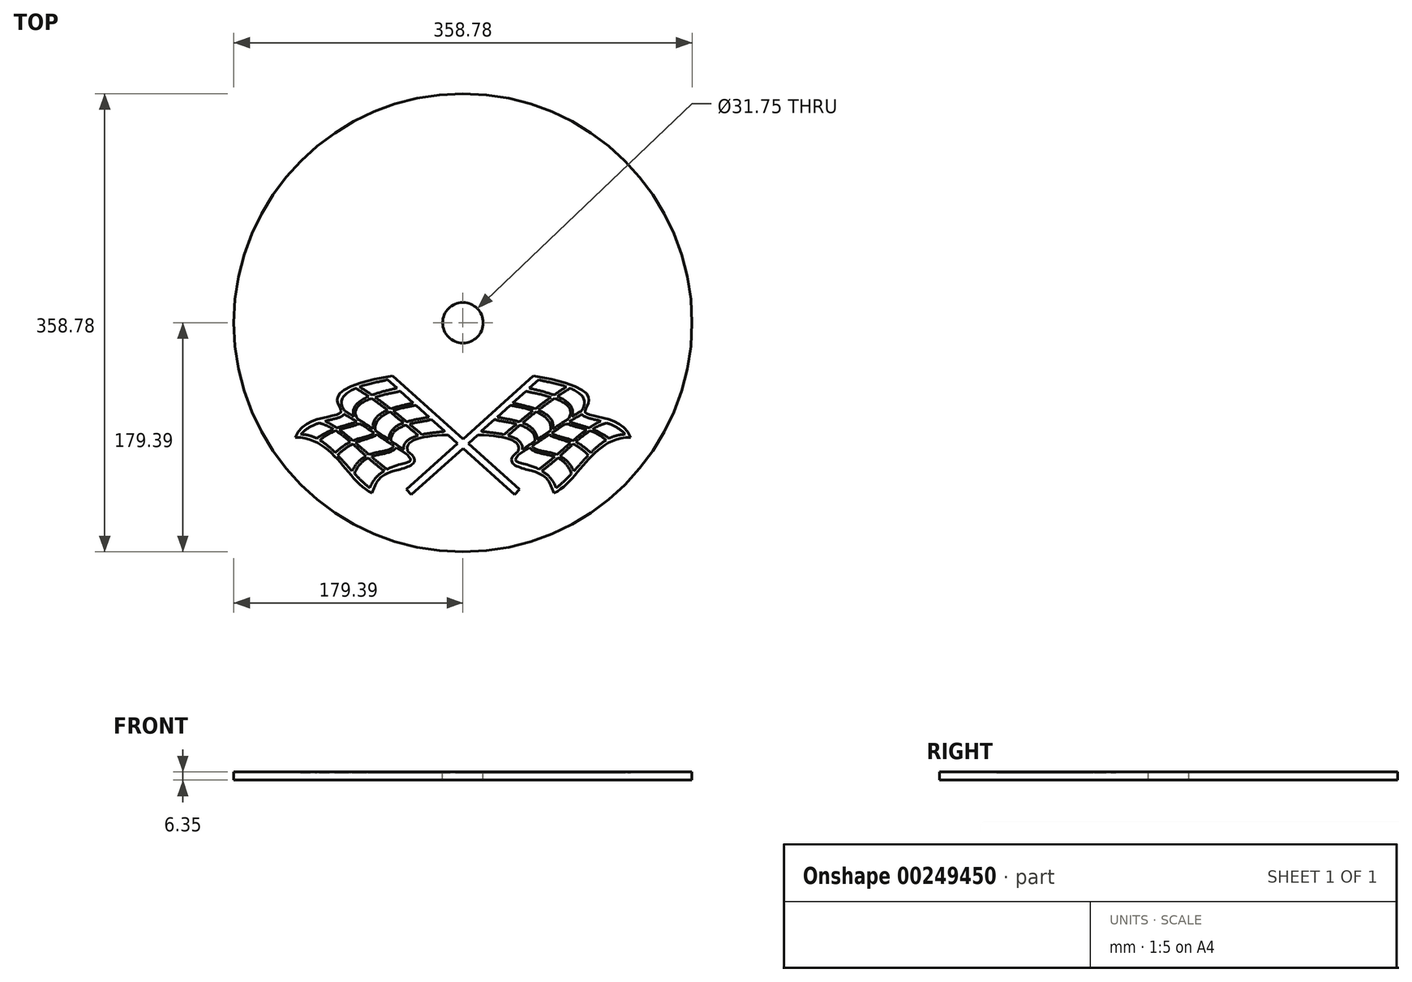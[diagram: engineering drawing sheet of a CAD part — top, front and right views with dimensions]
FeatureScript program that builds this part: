
annotation { "Feature Type Name" : "Feature", "Feature Type Description" : "" }
export const myFeature = defineFeature(function(context is Context, id is Id, definition is map)
    precondition{}
    {
        {
            var Q0;
            Q0=qCreatedBy(makeId("Top.planeOp"),FACE);
            var sketch = newSketch(context, id + "F0", { "sketchPlane" : qUnion([Q0])});
            skCircle(sketch, "E0", {"center": v(0, 0) * mm, "radius": 179.39 * mm});
            skSolve(sketch);
        }
        {
            var Q0;
            Q0=makeQuery(id+"F0.imprint","IMPRINT",FACE,{"disambiguationData":[TD([[makeQuery(id+"F0.imprint","IMPRINT",EDGE,{"derivedFrom":sQuery(id+"F0.wireOp",EDGE,"E0")}),1.0]])]});
            var sketch = newSketch(context, id + "F1", { "sketchPlane" : qUnion([Q0])});
            skCircle(sketch, "E1", {"center": v(0, 0) * mm, "radius": 15.88 * mm});
            skSolve(sketch);
        }
        {
            var Q0;
            Q0 = qSketchRegion(id + "F0", true);
            extrude(context, id + "F2", {"entities" : qUnion([Q0]), "oppositeDirection" : true, "depth" : 6.35 * mm});
        }
        {
            var Q0;
            Q0 = qSketchRegion(id + "F1", true);
            extrude(context, id + "F3", {"entities" : qUnion([Q0]), "operationType" : NewBodyOperationType.REMOVE, "oppositeDirection" : true, "depth" : 6.35 * mm});
        }
        {
            var Q0;
            Q0=makeQuery(id+"F2.opExtrude","CAP_FACE",FACE,{"disambiguationData":[OSD([sQuery(id+"F0.wireOp",EDGE,"E0")])],"isStart":true});
            var sketch = newSketch(context, id + "F4", { "sketchPlane" : qUnion([Q0])});
            skPoint(sketch, "E2", {"position": v(0, -89.7) * mm});
            skSolve(sketch);
        }
        {
            var Q0;
            Q0=makeQuery(id+"F4.imprint","IMPRINT",FACE,{"disambiguationData":[TD([[makeQuery(id+"F4.imprint","IMPRINT",EDGE,{"derivedFrom":makeQuery(id+"F2.opExtrude","CAP_EDGE",EDGE,{"disambiguationData":[OSD([sQuery(id+"F0.wireOp",EDGE,"E0")])],"isStart":true})}),1.0]])]});
            var sketch = newSketch(context, id + "F5", { "sketchPlane" : qUnion([Q0])});
            skLineSegment(sketch, "E3", {"start": v(0.06, -91) * mm, "end": v(55.08, -41.46) * mm});
            skLineSegment(sketch, "E4", {"start": v(0.06, -91) * mm, "end": v(0.06, -98.3) * mm});
            skLineSegment(sketch, "E5", {"start": v(40.53, -134.74) * mm, "end": v(0.06, -98.3) * mm});
            skLineSegment(sketch, "E6", {"start": v(4.24, -94.53) * mm, "end": v(44.28, -130.58) * mm});
            skLineSegment(sketch, "E7", {"start": v(44.28, -130.58) * mm, "end": v(40.53, -134.74) * mm});
            skLineSegment(sketch, "E8", {"start": v(4.24, -94.53) * mm, "end": v(11.6, -87.9) * mm});
            skFitSpline(sketch, "E9", {"points": [v(55.08, -41.46) * mm, v(95.8, -70.26) * mm, v(131.24, -89.78) * mm], "startDerivative": vector(364.2, -61.64) * mm, "endDerivative": vector(39.76, -111.19) * mm});
            skFitSpline(sketch, "E10", {"points": [v(71.44, -133.33) * mm, v(131.24, -89.78) * mm], "startDerivative": vector(60.45, 28.94) * mm, "endDerivative": vector(92, 0.58) * mm});
            skFitSpline(sketch, "E11", {"points": [v(11.6, -87.9) * mm, v(43.33, -100.64) * mm], "startDerivative": vector(115.17, -2.72) * mm, "endDerivative": vector(0.68, -4.6) * mm});
            skFitSpline(sketch, "E12", {"points": [v(43.33, -100.64) * mm, v(57.53, -117) * mm], "startDerivative": vector(-48.85, -36.41) * mm, "endDerivative": vector(12.7, -6.51) * mm});
            skFitSpline(sketch, "E13", {"points": [v(57.53, -117) * mm, v(71.44, -133.33) * mm], "startDerivative": vector(35.48, -14.65) * mm, "endDerivative": vector(10.45, -16.83) * mm});
            skLineSegment(sketch, "E14", {"start": v(59.43, -44.38) * mm, "end": v(14.42, -84.9) * mm});
            skFitSpline(sketch, "E15", {"points": [v(59.43, -44.38) * mm, v(92.63, -69.16) * mm], "startDerivative": vector(4.23, -5.68) * mm, "endDerivative": vector(-40.92, -57) * mm});
            skFitSpline(sketch, "E16", {"points": [v(92.63, -69.16) * mm, v(127.21, -87.43) * mm], "startDerivative": vector(-2.56, -25.58) * mm, "endDerivative": vector(40.92, -43.11) * mm});
            skFitSpline(sketch, "E17", {"points": [v(127.21, -87.43) * mm, v(73.02, -129.33) * mm], "startDerivative": vector(-65.77, 0.73) * mm, "endDerivative": vector(-53.9, -39.85) * mm});
            skFitSpline(sketch, "E18", {"points": [v(73.02, -129.33) * mm, v(59.49, -114.78) * mm], "startDerivative": vector(-15.42, 35.71) * mm, "endDerivative": vector(-6.55, 5.86) * mm});
            skFitSpline(sketch, "E19", {"points": [v(45.58, -101.9) * mm, v(14.42, -84.9) * mm], "startDerivative": vector(22.35, 49.66) * mm, "endDerivative": vector(-0.57, 3.77) * mm});
            skFitSpline(sketch, "E20", {"points": [v(59.49, -114.78) * mm, v(41.53, -108.23) * mm, v(45.58, -101.9) * mm], "startDerivative": vector(-46.67, 24.68) * mm, "endDerivative": vector(28.86, 20.59) * mm});
            skFitSpline(sketch, "E21", {"points": [v(32.25, -87.53) * mm, v(81.1, -50.15) * mm], "startDerivative": vector(50.96, 43.08) * mm, "endDerivative": vector(51.1, 31.8) * mm});
            skFitSpline(sketch, "E22", {"points": [v(84, -51.27) * mm, v(35.3, -88.3) * mm], "startDerivative": vector(-51.19, -30.53) * mm, "endDerivative": vector(-43.5, -39.18) * mm});
            skFitSpline(sketch, "E23", {"points": [v(45.58, -101.9) * mm, v(93.2, -71.67) * mm], "startDerivative": vector(25.12, 14.48) * mm, "endDerivative": vector(41.52, 21.74) * mm});
            skFitSpline(sketch, "E24", {"points": [v(92.63, -69.16) * mm, v(46.4, -99.35) * mm], "startDerivative": vector(-45.64, -26.15) * mm, "endDerivative": vector(-46.22, -30.19) * mm});
            skFitSpline(sketch, "E25", {"points": [v(59.49, -114.78) * mm, v(108.1, -77.03) * mm], "startDerivative": vector(57.5, 42.76) * mm, "endDerivative": vector(45.15, 20.14) * mm});
            skFitSpline(sketch, "E26", {"points": [v(112.62, -78.42) * mm, v(61.67, -116.13) * mm], "startDerivative": vector(-55.23, -15.98) * mm, "endDerivative": vector(-62.07, -45.79) * mm});
            skFitSpline(sketch, "E27", {"points": [v(51.8, -51.24) * mm, v(85.23, -73.58) * mm], "startDerivative": vector(59.56, -12.69) * mm, "endDerivative": vector(-14.16, -35.72) * mm});
            skFitSpline(sketch, "E28", {"points": [v(82.9, -75.03) * mm, v(49.25, -53.54) * mm], "startDerivative": vector(27, 46.28) * mm, "endDerivative": vector(-17.19, 5.44) * mm});
            skFitSpline(sketch, "E29", {"points": [v(39.05, -62.73) * mm, v(70.31, -83.27) * mm], "startDerivative": vector(11.23, -4.77) * mm, "endDerivative": vector(-10.96, -46.85) * mm});
            skFitSpline(sketch, "E30", {"points": [v(68.66, -84.37) * mm, v(36.92, -64.64) * mm], "startDerivative": vector(7.96, 47.76) * mm, "endDerivative": vector(-8.63, 2.48) * mm});
            skFitSpline(sketch, "E31", {"points": [v(26.7, -73.84) * mm, v(58.1, -91.53) * mm], "startDerivative": vector(37.58, -7.97) * mm, "endDerivative": vector(0.75, -41.64) * mm});
            skFitSpline(sketch, "E32", {"points": [v(56.34, -92.73) * mm, v(24.88, -75.49) * mm], "startDerivative": vector(4.56, 45.23) * mm, "endDerivative": vector(-8.2, 7.87) * mm});
            skFitSpline(sketch, "E33", {"points": [v(83.27, -77.43) * mm, v(114.61, -90.56) * mm], "startDerivative": vector(38.14, -14.1) * mm, "endDerivative": vector(43.15, -28.8) * mm});
            skFitSpline(sketch, "E34", {"points": [v(112.08, -91.98) * mm, v(80.88, -78.92) * mm], "startDerivative": vector(-31.06, 28.3) * mm, "endDerivative": vector(-31.22, 13.08) * mm});
            skFitSpline(sketch, "E35", {"points": [v(100.17, -101.75) * mm, v(69.48, -86.28) * mm], "startDerivative": vector(-46.77, 41.89) * mm, "endDerivative": vector(-28.56, 17.74) * mm});
            skFitSpline(sketch, "E36", {"points": [v(67.37, -87.68) * mm, v(98.28, -103.67) * mm], "startDerivative": vector(30.92, -16) * mm, "endDerivative": vector(36.35, -35.94) * mm});
            skFitSpline(sketch, "E37", {"points": [v(86.88, -116.17) * mm, v(54.19, -96.44) * mm], "startDerivative": vector(-26.62, 57.68) * mm, "endDerivative": vector(-13.53, 22.22) * mm});
            skFitSpline(sketch, "E38", {"points": [v(52.08, -97.83) * mm, v(85.09, -118.11) * mm], "startDerivative": vector(26.1, -26.3) * mm, "endDerivative": vector(24.75, -58.52) * mm});
            skLineSegment(sketch, "E39.MirrorCS", {"start": v(-44.17, -130.58) * mm, "end": v(-40.42, -134.74) * mm});
            skFitSpline(sketch, "E40.MirrorCS", {"points": [v(-59.38, -114.78) * mm, v(-41.42, -108.23) * mm, v(-45.47, -101.9) * mm], "startDerivative": vector(46.67, 24.68) * mm, "endDerivative": vector(-28.86, 20.59) * mm});
            skFitSpline(sketch, "E41.MirrorCS", {"points": [v(-111.97, -91.98) * mm, v(-80.77, -78.92) * mm], "startDerivative": vector(31.06, 28.3) * mm, "endDerivative": vector(31.22, 13.08) * mm});
            skFitSpline(sketch, "E42.MirrorCS", {"points": [v(-72.9, -129.33) * mm, v(-59.38, -114.78) * mm], "startDerivative": vector(15.42, 35.71) * mm, "endDerivative": vector(6.55, 5.86) * mm});
            skFitSpline(sketch, "E43.MirrorCS", {"points": [v(-83.16, -77.43) * mm, v(-114.5, -90.56) * mm], "startDerivative": vector(-38.14, -14.1) * mm, "endDerivative": vector(-43.15, -28.8) * mm});
            skFitSpline(sketch, "E44.MirrorCS", {"points": [v(-57.42, -117) * mm, v(-71.33, -133.33) * mm], "startDerivative": vector(-35.48, -14.65) * mm, "endDerivative": vector(-10.45, -16.83) * mm});
            skFitSpline(sketch, "E45.MirrorCS", {"points": [v(-92.52, -69.16) * mm, v(-46.29, -99.35) * mm], "startDerivative": vector(45.64, -26.15) * mm, "endDerivative": vector(46.22, -30.19) * mm});
            skFitSpline(sketch, "E46.MirrorCS", {"points": [v(-100.06, -101.75) * mm, v(-69.37, -86.28) * mm], "startDerivative": vector(46.77, 41.89) * mm, "endDerivative": vector(28.56, 17.74) * mm});
            skFitSpline(sketch, "E47.MirrorCS", {"points": [v(-82.8, -75.03) * mm, v(-49.14, -53.54) * mm], "startDerivative": vector(-27, 46.28) * mm, "endDerivative": vector(17.19, 5.44) * mm});
            skFitSpline(sketch, "E48.MirrorCS", {"points": [v(-45.47, -101.9) * mm, v(-14.3, -84.9) * mm], "startDerivative": vector(-22.35, 49.66) * mm, "endDerivative": vector(0.57, 3.77) * mm});
            skFitSpline(sketch, "E49.MirrorCS", {"points": [v(-112.5, -78.42) * mm, v(-61.56, -116.13) * mm], "startDerivative": vector(55.23, -15.98) * mm, "endDerivative": vector(62.07, -45.79) * mm});
            skFitSpline(sketch, "E50.MirrorCS", {"points": [v(-51.7, -51.24) * mm, v(-85.12, -73.58) * mm], "startDerivative": vector(-59.56, -12.69) * mm, "endDerivative": vector(14.16, -35.72) * mm});
            skFitSpline(sketch, "E51.MirrorCS", {"points": [v(-59.32, -44.38) * mm, v(-92.52, -69.16) * mm], "startDerivative": vector(-4.23, -5.68) * mm, "endDerivative": vector(40.92, -57) * mm});
            skFitSpline(sketch, "E52.MirrorCS", {"points": [v(-83.9, -51.27) * mm, v(-35.2, -88.3) * mm], "startDerivative": vector(51.19, -30.53) * mm, "endDerivative": vector(43.5, -39.18) * mm});
            skFitSpline(sketch, "E53.MirrorCS", {"points": [v(-59.38, -114.78) * mm, v(-108, -77.03) * mm], "startDerivative": vector(-57.5, 42.76) * mm, "endDerivative": vector(-45.15, 20.14) * mm});
            skFitSpline(sketch, "E54.MirrorCS", {"points": [v(-11.48, -87.9) * mm, v(-43.22, -100.64) * mm], "startDerivative": vector(-115.17, -2.72) * mm, "endDerivative": vector(-0.68, -4.6) * mm});
            skFitSpline(sketch, "E55.MirrorCS", {"points": [v(-71.33, -133.33) * mm, v(-131.13, -89.78) * mm], "startDerivative": vector(-60.45, 28.94) * mm, "endDerivative": vector(-92, 0.58) * mm});
            skFitSpline(sketch, "E56.MirrorCS", {"points": [v(-54.97, -41.46) * mm, v(-95.68, -70.26) * mm, v(-131.13, -89.78) * mm], "startDerivative": vector(-364.2, -61.64) * mm, "endDerivative": vector(-39.76, -111.19) * mm});
            skLineSegment(sketch, "E57.MirrorCS", {"start": v(-4.13, -94.53) * mm, "end": v(-11.48, -87.9) * mm});
            skFitSpline(sketch, "E58.MirrorCS", {"points": [v(-51.97, -97.83) * mm, v(-84.98, -118.11) * mm], "startDerivative": vector(-26.1, -26.3) * mm, "endDerivative": vector(-24.75, -58.52) * mm});
            skLineSegment(sketch, "E59.MirrorCS", {"start": v(-4.13, -94.53) * mm, "end": v(-44.17, -130.58) * mm});
            skLineSegment(sketch, "E60.MirrorCS", {"start": v(-40.42, -134.74) * mm, "end": v(0.06, -98.3) * mm});
            skLineSegment(sketch, "E61.MirrorCS", {"start": v(0.06, -91) * mm, "end": v(-54.97, -41.46) * mm});
            skLineSegment(sketch, "E62.MirrorCS", {"start": v(-59.32, -44.38) * mm, "end": v(-14.3, -84.9) * mm});
            skFitSpline(sketch, "E63.MirrorCS", {"points": [v(-127.1, -87.43) * mm, v(-72.9, -129.33) * mm], "startDerivative": vector(65.77, 0.73) * mm, "endDerivative": vector(53.9, -39.85) * mm});
            skFitSpline(sketch, "E64.MirrorCS", {"points": [v(-43.22, -100.64) * mm, v(-57.42, -117) * mm], "startDerivative": vector(48.85, -36.41) * mm, "endDerivative": vector(-12.7, -6.51) * mm});
            skFitSpline(sketch, "E65.MirrorCS", {"points": [v(-56.23, -92.73) * mm, v(-24.77, -75.49) * mm], "startDerivative": vector(-4.56, 45.23) * mm, "endDerivative": vector(8.2, 7.87) * mm});
            skFitSpline(sketch, "E66.MirrorCS", {"points": [v(-26.59, -73.84) * mm, v(-58, -91.53) * mm], "startDerivative": vector(-37.58, -7.97) * mm, "endDerivative": vector(-0.75, -41.64) * mm});
            skFitSpline(sketch, "E67.MirrorCS", {"points": [v(-68.55, -84.37) * mm, v(-36.81, -64.64) * mm], "startDerivative": vector(-7.96, 47.76) * mm, "endDerivative": vector(8.63, 2.48) * mm});
            skFitSpline(sketch, "E68.MirrorCS", {"points": [v(-86.77, -116.17) * mm, v(-54.07, -96.44) * mm], "startDerivative": vector(26.62, 57.68) * mm, "endDerivative": vector(13.53, 22.22) * mm});
            skFitSpline(sketch, "E69.MirrorCS", {"points": [v(-32.13, -87.53) * mm, v(-81, -50.15) * mm], "startDerivative": vector(-50.96, 43.08) * mm, "endDerivative": vector(-51.1, 31.8) * mm});
            skFitSpline(sketch, "E70.MirrorCS", {"points": [v(-92.52, -69.16) * mm, v(-127.1, -87.43) * mm], "startDerivative": vector(2.56, -25.58) * mm, "endDerivative": vector(-40.92, -43.11) * mm});
            skFitSpline(sketch, "E71.MirrorCS", {"points": [v(-45.47, -101.9) * mm, v(-93.1, -71.67) * mm], "startDerivative": vector(-25.12, 14.48) * mm, "endDerivative": vector(-41.52, 21.74) * mm});
            skFitSpline(sketch, "E72.MirrorCS", {"points": [v(-38.94, -62.73) * mm, v(-70.2, -83.27) * mm], "startDerivative": vector(-11.23, -4.77) * mm, "endDerivative": vector(10.96, -46.85) * mm});
            skFitSpline(sketch, "E73.MirrorCS", {"points": [v(-67.26, -87.68) * mm, v(-98.17, -103.67) * mm], "startDerivative": vector(-30.92, -16) * mm, "endDerivative": vector(-36.35, -35.94) * mm});
            skLineSegment(sketch, "E74", {"start": v(4.24, -94.53) * mm, "end": v(0.06, -98.3) * mm});
            skSolve(sketch);
        }
        {
            var Q0;
            Q0 = qSketchRegion(id + "F5", true);
            var Q1;
            {var subQ0=sQuery(id+"F5.wireOp",EDGE,"E53.MirrorCS");var subQ1=sQuery(id+"F5.wireOp",EDGE,"E43.MirrorCS");var subQ2=makeQuery(id+"F5.imprint","INTERSECT",VERTEX,{"derivedFrom":[subQ1,subQ0]});Q1=makeQuery(id+"F5.imprint","IMPRINT",FACE,{"disambiguationData":[TD([[makeQuery(id+"F5.imprint","IMPRINT",EDGE,{"disambiguationData":[TD([[subQ2,-1.0]])],"derivedFrom":subQ1}),-1.0]])]});}
            var Q2;
            {var subQ0=sQuery(id+"F5.wireOp",EDGE,"E63.MirrorCS");var subQ1=sQuery(id+"F5.wireOp",EDGE,"E41.MirrorCS");var subQ2=makeQuery(id+"F5.imprint","INTERSECT",VERTEX,{"derivedFrom":[subQ1,subQ0]});Q2=makeQuery(id+"F5.imprint","IMPRINT",FACE,{"disambiguationData":[TD([[makeQuery(id+"F5.imprint","IMPRINT",EDGE,{"disambiguationData":[TD([[subQ2,-1.0]])],"derivedFrom":subQ1}),1.0]])]});}
            var Q3;
            {var subQ0=sQuery(id+"F5.wireOp",EDGE,"E49.MirrorCS");var subQ1=sQuery(id+"F5.wireOp",EDGE,"E41.MirrorCS");var subQ2=makeQuery(id+"F5.imprint","INTERSECT",VERTEX,{"derivedFrom":[subQ1,subQ0]});Q3=makeQuery(id+"F5.imprint","IMPRINT",FACE,{"disambiguationData":[TD([[makeQuery(id+"F5.imprint","IMPRINT",EDGE,{"disambiguationData":[TD([[subQ2,-1.0]])],"derivedFrom":subQ1}),1.0]])]});}
            var Q4;
            {var subQ0=sQuery(id+"F5.wireOp",EDGE,"E71.MirrorCS");var subQ1=sQuery(id+"F5.wireOp",EDGE,"E41.MirrorCS");var subQ2=makeQuery(id+"F5.imprint","INTERSECT",VERTEX,{"derivedFrom":[subQ1,subQ0]});Q4=makeQuery(id+"F5.imprint","IMPRINT",FACE,{"disambiguationData":[TD([[makeQuery(id+"F5.imprint","IMPRINT",EDGE,{"disambiguationData":[TD([[subQ2,1.0]])],"derivedFrom":subQ1}),1.0]])]});}
            var Q5;
            {var subQ0=sQuery(id+"F5.wireOp",EDGE,"E49.MirrorCS");var subQ1=sQuery(id+"F5.wireOp",EDGE,"E41.MirrorCS");var subQ2=makeQuery(id+"F5.imprint","INTERSECT",VERTEX,{"derivedFrom":[subQ1,subQ0]});Q5=makeQuery(id+"F5.imprint","IMPRINT",FACE,{"disambiguationData":[TD([[makeQuery(id+"F5.imprint","IMPRINT",EDGE,{"disambiguationData":[TD([[subQ2,-1.0]])],"derivedFrom":subQ1}),-1.0]])]});}
            var Q6;
            {var subQ0=sQuery(id+"F5.wireOp",EDGE,"E49.MirrorCS");var subQ1=sQuery(id+"F5.wireOp",EDGE,"E46.MirrorCS");var subQ2=makeQuery(id+"F5.imprint","INTERSECT",VERTEX,{"derivedFrom":[subQ1,subQ0]});Q6=makeQuery(id+"F5.imprint","IMPRINT",FACE,{"disambiguationData":[TD([[makeQuery(id+"F5.imprint","IMPRINT",EDGE,{"disambiguationData":[TD([[subQ2,-1.0]])],"derivedFrom":subQ1}),-1.0]])]});}
            var Q7;
            {var subQ0=sQuery(id+"F5.wireOp",EDGE,"E63.MirrorCS");var subQ1=sQuery(id+"F5.wireOp",EDGE,"E46.MirrorCS");var subQ2=makeQuery(id+"F5.imprint","INTERSECT",VERTEX,{"derivedFrom":[subQ1,subQ0]});Q7=makeQuery(id+"F5.imprint","IMPRINT",FACE,{"disambiguationData":[TD([[makeQuery(id+"F5.imprint","IMPRINT",EDGE,{"disambiguationData":[TD([[subQ2,-1.0]])],"derivedFrom":subQ1}),-1.0]])]});}
            var Q8;
            {var subQ0=sQuery(id+"F5.wireOp",EDGE,"E71.MirrorCS");var subQ1=sQuery(id+"F5.wireOp",EDGE,"E46.MirrorCS");var subQ2=makeQuery(id+"F5.imprint","INTERSECT",VERTEX,{"derivedFrom":[subQ1,subQ0]});Q8=makeQuery(id+"F5.imprint","IMPRINT",FACE,{"disambiguationData":[TD([[makeQuery(id+"F5.imprint","IMPRINT",EDGE,{"disambiguationData":[TD([[subQ2,1.0]])],"derivedFrom":subQ1}),-1.0]])]});}
            var Q9;
            {var subQ0=sQuery(id+"F5.wireOp",EDGE,"E73.MirrorCS");var subQ1=sQuery(id+"F5.wireOp",EDGE,"E49.MirrorCS");var subQ2=makeQuery(id+"F5.imprint","INTERSECT",VERTEX,{"derivedFrom":[subQ1,subQ0]});Q9=makeQuery(id+"F5.imprint","IMPRINT",FACE,{"disambiguationData":[TD([[makeQuery(id+"F5.imprint","IMPRINT",EDGE,{"disambiguationData":[TD([[subQ2,-1.0]])],"derivedFrom":subQ1}),1.0]])]});}
            var Q10;
            {var subQ0=sQuery(id+"F5.wireOp",EDGE,"E68.MirrorCS");var subQ1=sQuery(id+"F5.wireOp",EDGE,"E49.MirrorCS");var subQ2=makeQuery(id+"F5.imprint","INTERSECT",VERTEX,{"derivedFrom":[subQ1,subQ0]});Q10=makeQuery(id+"F5.imprint","IMPRINT",FACE,{"disambiguationData":[TD([[makeQuery(id+"F5.imprint","IMPRINT",EDGE,{"disambiguationData":[TD([[subQ2,-1.0]])],"derivedFrom":subQ1}),1.0]])]});}
            var Q11;
            {var subQ0=sQuery(id+"F5.wireOp",EDGE,"E68.MirrorCS");var subQ1=sQuery(id+"F5.wireOp",EDGE,"E49.MirrorCS");var subQ2=makeQuery(id+"F5.imprint","INTERSECT",VERTEX,{"derivedFrom":[subQ1,subQ0]});Q11=makeQuery(id+"F5.imprint","IMPRINT",FACE,{"disambiguationData":[TD([[makeQuery(id+"F5.imprint","IMPRINT",EDGE,{"disambiguationData":[TD([[subQ2,-1.0]])],"derivedFrom":subQ1}),-1.0]])]});}
            var Q12;
            {var subQ0=sQuery(id+"F5.wireOp",EDGE,"E58.MirrorCS");var subQ1=sQuery(id+"F5.wireOp",EDGE,"E53.MirrorCS");var subQ2=makeQuery(id+"F5.imprint","INTERSECT",VERTEX,{"derivedFrom":[subQ1,subQ0]});Q12=makeQuery(id+"F5.imprint","IMPRINT",FACE,{"disambiguationData":[TD([[makeQuery(id+"F5.imprint","IMPRINT",EDGE,{"disambiguationData":[TD([[subQ2,-1.0]])],"derivedFrom":subQ1}),-1.0]])]});}
            var Q13;
            {var subQ1=sQuery(id+"F5.wireOp",EDGE,"E42.MirrorCS");var subQ3=sQuery(id+"F5.wireOp",EDGE,"E49.MirrorCS");var subQ4=makeQuery(id+"F5.imprint","INTERSECT",VERTEX,{"derivedFrom":[subQ1,subQ3]});Q13=makeQuery(id+"F5.imprint","IMPRINT",FACE,{"disambiguationData":[TD([[makeQuery(id+"F5.imprint","IMPRINT",EDGE,{"disambiguationData":[TD([[subQ4,1.0]])],"derivedFrom":subQ3}),1.0]])]});}
            var Q14;
            {var subQ1=sQuery(id+"F5.wireOp",EDGE,"E45.MirrorCS");var subQ13=makeQuery(id+"F5.imprint","INTERSECT",VERTEX,{"derivedFrom":[subQ1,sQuery(id+"F5.wireOp",EDGE,"E47.MirrorCS")]});Q14=makeQuery(id+"F5.imprint","IMPRINT",FACE,{"disambiguationData":[TD([[makeQuery(id+"F5.imprint","IMPRINT",EDGE,{"disambiguationData":[TD([[subQ13,1.0]])],"derivedFrom":subQ1}),-1.0]])]});}
            var Q15;
            {var subQ0=sQuery(id+"F5.wireOp",EDGE,"E65.MirrorCS");var subQ1=sQuery(id+"F5.wireOp",EDGE,"E45.MirrorCS");var subQ2=makeQuery(id+"F5.imprint","INTERSECT",VERTEX,{"derivedFrom":[subQ1,subQ0]});Q15=makeQuery(id+"F5.imprint","IMPRINT",FACE,{"disambiguationData":[TD([[makeQuery(id+"F5.imprint","IMPRINT",EDGE,{"disambiguationData":[TD([[subQ2,1.0]])],"derivedFrom":subQ1}),1.0]])]});}
            var Q16;
            {var subQ0=sQuery(id+"F5.wireOp",EDGE,"E67.MirrorCS");var subQ1=sQuery(id+"F5.wireOp",EDGE,"E45.MirrorCS");var subQ2=makeQuery(id+"F5.imprint","INTERSECT",VERTEX,{"derivedFrom":[subQ1,subQ0]});Q16=makeQuery(id+"F5.imprint","IMPRINT",FACE,{"disambiguationData":[TD([[makeQuery(id+"F5.imprint","IMPRINT",EDGE,{"disambiguationData":[TD([[subQ2,1.0]])],"derivedFrom":subQ1}),1.0]])]});}
            var Q17;
            {var subQ0=sQuery(id+"F5.wireOp",EDGE,"E47.MirrorCS");var subQ1=sQuery(id+"F5.wireOp",EDGE,"E45.MirrorCS");var subQ2=makeQuery(id+"F5.imprint","INTERSECT",VERTEX,{"derivedFrom":[subQ1,subQ0]});Q17=makeQuery(id+"F5.imprint","IMPRINT",FACE,{"disambiguationData":[TD([[makeQuery(id+"F5.imprint","IMPRINT",EDGE,{"disambiguationData":[TD([[subQ2,1.0]])],"derivedFrom":subQ1}),1.0]])]});}
            var Q18;
            {var subQ0=sQuery(id+"F5.wireOp",EDGE,"E69.MirrorCS");var subQ1=sQuery(id+"F5.wireOp",EDGE,"E50.MirrorCS");var subQ2=makeQuery(id+"F5.imprint","INTERSECT",VERTEX,{"derivedFrom":[subQ1,subQ0]});Q18=makeQuery(id+"F5.imprint","IMPRINT",FACE,{"disambiguationData":[TD([[makeQuery(id+"F5.imprint","IMPRINT",EDGE,{"disambiguationData":[TD([[subQ2,-1.0]])],"derivedFrom":subQ1}),-1.0]])]});}
            var Q19;
            {var subQ0=sQuery(id+"F5.wireOp",EDGE,"E52.MirrorCS");var subQ1=sQuery(id+"F5.wireOp",EDGE,"E47.MirrorCS");var subQ2=makeQuery(id+"F5.imprint","INTERSECT",VERTEX,{"derivedFrom":[subQ1,subQ0]});Q19=makeQuery(id+"F5.imprint","IMPRINT",FACE,{"disambiguationData":[TD([[makeQuery(id+"F5.imprint","IMPRINT",EDGE,{"disambiguationData":[TD([[subQ2,-1.0]])],"derivedFrom":subQ1}),1.0]])]});}
            var Q20;
            {var subQ0=sQuery(id+"F5.wireOp",EDGE,"E62.MirrorCS");var subQ1=sQuery(id+"F5.wireOp",EDGE,"E47.MirrorCS");var subQ2=makeQuery(id+"F5.imprint","INTERSECT",VERTEX,{"derivedFrom":[subQ1,subQ0]});Q20=makeQuery(id+"F5.imprint","IMPRINT",FACE,{"disambiguationData":[TD([[makeQuery(id+"F5.imprint","IMPRINT",EDGE,{"disambiguationData":[TD([[subQ2,1.0]])],"derivedFrom":subQ1}),1.0]])]});}
            var Q21;
            {var subQ0=sQuery(id+"F5.wireOp",EDGE,"E52.MirrorCS");var subQ1=sQuery(id+"F5.wireOp",EDGE,"E47.MirrorCS");var subQ2=makeQuery(id+"F5.imprint","INTERSECT",VERTEX,{"derivedFrom":[subQ1,subQ0]});Q21=makeQuery(id+"F5.imprint","IMPRINT",FACE,{"disambiguationData":[TD([[makeQuery(id+"F5.imprint","IMPRINT",EDGE,{"disambiguationData":[TD([[subQ2,-1.0]])],"derivedFrom":subQ1}),-1.0]])]});}
            var Q22;
            {var subQ0=sQuery(id+"F5.wireOp",EDGE,"E72.MirrorCS");var subQ1=sQuery(id+"F5.wireOp",EDGE,"E52.MirrorCS");var subQ2=makeQuery(id+"F5.imprint","INTERSECT",VERTEX,{"derivedFrom":[subQ1,subQ0]});Q22=makeQuery(id+"F5.imprint","IMPRINT",FACE,{"disambiguationData":[TD([[makeQuery(id+"F5.imprint","IMPRINT",EDGE,{"disambiguationData":[TD([[subQ2,-1.0]])],"derivedFrom":subQ1}),1.0]])]});}
            var Q23;
            {var subQ0=sQuery(id+"F5.wireOp",EDGE,"E67.MirrorCS");var subQ1=sQuery(id+"F5.wireOp",EDGE,"E62.MirrorCS");var subQ2=makeQuery(id+"F5.imprint","INTERSECT",VERTEX,{"derivedFrom":[subQ1,subQ0]});Q23=makeQuery(id+"F5.imprint","IMPRINT",FACE,{"disambiguationData":[TD([[makeQuery(id+"F5.imprint","IMPRINT",EDGE,{"disambiguationData":[TD([[subQ2,1.0]])],"derivedFrom":subQ1}),-1.0]])]});}
            var Q24;
            {var subQ0=sQuery(id+"F5.wireOp",EDGE,"E67.MirrorCS");var subQ1=sQuery(id+"F5.wireOp",EDGE,"E52.MirrorCS");var subQ2=makeQuery(id+"F5.imprint","INTERSECT",VERTEX,{"derivedFrom":[subQ1,subQ0]});Q24=makeQuery(id+"F5.imprint","IMPRINT",FACE,{"disambiguationData":[TD([[makeQuery(id+"F5.imprint","IMPRINT",EDGE,{"disambiguationData":[TD([[subQ2,-1.0]])],"derivedFrom":subQ1}),1.0]])]});}
            var Q25;
            {var subQ0=sQuery(id+"F5.wireOp",EDGE,"E66.MirrorCS");var subQ1=sQuery(id+"F5.wireOp",EDGE,"E52.MirrorCS");var subQ2=makeQuery(id+"F5.imprint","INTERSECT",VERTEX,{"derivedFrom":[subQ1,subQ0]});Q25=makeQuery(id+"F5.imprint","IMPRINT",FACE,{"disambiguationData":[TD([[makeQuery(id+"F5.imprint","IMPRINT",EDGE,{"disambiguationData":[TD([[subQ2,-1.0]])],"derivedFrom":subQ1}),1.0]])]});}
            var Q26;
            {var subQ0=sQuery(id+"F5.wireOp",EDGE,"E65.MirrorCS");var subQ1=sQuery(id+"F5.wireOp",EDGE,"E62.MirrorCS");var subQ2=makeQuery(id+"F5.imprint","INTERSECT",VERTEX,{"derivedFrom":[subQ1,subQ0]});Q26=makeQuery(id+"F5.imprint","IMPRINT",FACE,{"disambiguationData":[TD([[makeQuery(id+"F5.imprint","IMPRINT",EDGE,{"disambiguationData":[TD([[subQ2,1.0]])],"derivedFrom":subQ1}),-1.0]])]});}
            var Q27;
            {var subQ0=sQuery(id+"F5.wireOp",EDGE,"E52.MirrorCS");var subQ1=sQuery(id+"F5.wireOp",EDGE,"E48.MirrorCS");var subQ2=makeQuery(id+"F5.imprint","INTERSECT",VERTEX,{"derivedFrom":[subQ1,subQ0]});Q27=makeQuery(id+"F5.imprint","IMPRINT",FACE,{"disambiguationData":[TD([[makeQuery(id+"F5.imprint","IMPRINT",EDGE,{"disambiguationData":[TD([[subQ2,-1.0]])],"derivedFrom":subQ1}),1.0]])]});}
            var Q28;
            {var subQ0=sQuery(id+"F5.wireOp",EDGE,"E21");var subQ1=sQuery(id+"F5.wireOp",EDGE,"E19");var subQ2=makeQuery(id+"F5.imprint","INTERSECT",VERTEX,{"derivedFrom":[subQ1,subQ0]});Q28=makeQuery(id+"F5.imprint","IMPRINT",FACE,{"disambiguationData":[TD([[makeQuery(id+"F5.imprint","IMPRINT",EDGE,{"disambiguationData":[TD([[subQ2,1.0]])],"derivedFrom":subQ1}),-1.0]])]});}
            var Q29;
            {var subQ0=sQuery(id+"F5.wireOp",EDGE,"E31");var subQ1=sQuery(id+"F5.wireOp",EDGE,"E14");var subQ2=makeQuery(id+"F5.imprint","INTERSECT",VERTEX,{"derivedFrom":[subQ1,subQ0]});Q29=makeQuery(id+"F5.imprint","IMPRINT",FACE,{"disambiguationData":[TD([[makeQuery(id+"F5.imprint","IMPRINT",EDGE,{"disambiguationData":[TD([[subQ2,-1.0]])],"derivedFrom":subQ1}),1.0]])]});}
            var Q30;
            {var subQ0=sQuery(id+"F5.wireOp",EDGE,"E32");var subQ1=sQuery(id+"F5.wireOp",EDGE,"E21");var subQ2=makeQuery(id+"F5.imprint","INTERSECT",VERTEX,{"derivedFrom":[subQ1,subQ0]});Q30=makeQuery(id+"F5.imprint","IMPRINT",FACE,{"disambiguationData":[TD([[makeQuery(id+"F5.imprint","IMPRINT",EDGE,{"disambiguationData":[TD([[subQ2,-1.0]])],"derivedFrom":subQ1}),-1.0]])]});}
            var Q31;
            {var subQ0=sQuery(id+"F5.wireOp",EDGE,"E31");var subQ1=sQuery(id+"F5.wireOp",EDGE,"E21");var subQ2=makeQuery(id+"F5.imprint","INTERSECT",VERTEX,{"derivedFrom":[subQ1,subQ0]});Q31=makeQuery(id+"F5.imprint","IMPRINT",FACE,{"disambiguationData":[TD([[makeQuery(id+"F5.imprint","IMPRINT",EDGE,{"disambiguationData":[TD([[subQ2,-1.0]])],"derivedFrom":subQ1}),-1.0]])]});}
            var Q32;
            {var subQ0=sQuery(id+"F5.wireOp",EDGE,"E29");var subQ1=sQuery(id+"F5.wireOp",EDGE,"E14");var subQ2=makeQuery(id+"F5.imprint","INTERSECT",VERTEX,{"derivedFrom":[subQ1,subQ0]});Q32=makeQuery(id+"F5.imprint","IMPRINT",FACE,{"disambiguationData":[TD([[makeQuery(id+"F5.imprint","IMPRINT",EDGE,{"disambiguationData":[TD([[subQ2,-1.0]])],"derivedFrom":subQ1}),1.0]])]});}
            var Q33;
            {var subQ0=sQuery(id+"F5.wireOp",EDGE,"E27");var subQ1=sQuery(id+"F5.wireOp",EDGE,"E14");var subQ2=makeQuery(id+"F5.imprint","INTERSECT",VERTEX,{"derivedFrom":[subQ1,subQ0]});Q33=makeQuery(id+"F5.imprint","IMPRINT",FACE,{"disambiguationData":[TD([[makeQuery(id+"F5.imprint","IMPRINT",EDGE,{"disambiguationData":[TD([[subQ2,-1.0]])],"derivedFrom":subQ1}),1.0]])]});}
            var Q34;
            {var subQ0=sQuery(id+"F5.wireOp",EDGE,"E21");var subQ1=sQuery(id+"F5.wireOp",EDGE,"E15");var subQ2=makeQuery(id+"F5.imprint","INTERSECT",VERTEX,{"derivedFrom":[subQ1,subQ0]});Q34=makeQuery(id+"F5.imprint","IMPRINT",FACE,{"disambiguationData":[TD([[makeQuery(id+"F5.imprint","IMPRINT",EDGE,{"disambiguationData":[TD([[subQ2,-1.0]])],"derivedFrom":subQ1}),-1.0]])]});}
            var Q35;
            {var subQ0=sQuery(id+"F5.wireOp",EDGE,"E28");var subQ1=sQuery(id+"F5.wireOp",EDGE,"E21");var subQ2=makeQuery(id+"F5.imprint","INTERSECT",VERTEX,{"derivedFrom":[subQ1,subQ0]});Q35=makeQuery(id+"F5.imprint","IMPRINT",FACE,{"disambiguationData":[TD([[makeQuery(id+"F5.imprint","IMPRINT",EDGE,{"disambiguationData":[TD([[subQ2,-1.0]])],"derivedFrom":subQ1}),-1.0]])]});}
            var Q36;
            {var subQ0=sQuery(id+"F5.wireOp",EDGE,"E29");var subQ1=sQuery(id+"F5.wireOp",EDGE,"E21");var subQ2=makeQuery(id+"F5.imprint","INTERSECT",VERTEX,{"derivedFrom":[subQ1,subQ0]});Q36=makeQuery(id+"F5.imprint","IMPRINT",FACE,{"disambiguationData":[TD([[makeQuery(id+"F5.imprint","IMPRINT",EDGE,{"disambiguationData":[TD([[subQ2,-1.0]])],"derivedFrom":subQ1}),-1.0]])]});}
            var Q37;
            {var subQ0=sQuery(id+"F5.wireOp",EDGE,"E27");var subQ1=sQuery(id+"F5.wireOp",EDGE,"E22");var subQ2=makeQuery(id+"F5.imprint","INTERSECT",VERTEX,{"derivedFrom":[subQ1,subQ0]});Q37=makeQuery(id+"F5.imprint","IMPRINT",FACE,{"disambiguationData":[TD([[makeQuery(id+"F5.imprint","IMPRINT",EDGE,{"disambiguationData":[TD([[subQ2,-1.0]])],"derivedFrom":subQ1}),1.0]])]});}
            var Q38;
            {var subQ0=sQuery(id+"F5.wireOp",EDGE,"E29");var subQ1=sQuery(id+"F5.wireOp",EDGE,"E22");var subQ2=makeQuery(id+"F5.imprint","INTERSECT",VERTEX,{"derivedFrom":[subQ1,subQ0]});Q38=makeQuery(id+"F5.imprint","IMPRINT",FACE,{"disambiguationData":[TD([[makeQuery(id+"F5.imprint","IMPRINT",EDGE,{"disambiguationData":[TD([[subQ2,-1.0]])],"derivedFrom":subQ1}),1.0]])]});}
            var Q39;
            {var subQ0=sQuery(id+"F5.wireOp",EDGE,"E30");var subQ1=sQuery(id+"F5.wireOp",EDGE,"E21");var subQ2=makeQuery(id+"F5.imprint","INTERSECT",VERTEX,{"derivedFrom":[subQ1,subQ0]});Q39=makeQuery(id+"F5.imprint","IMPRINT",FACE,{"disambiguationData":[TD([[makeQuery(id+"F5.imprint","IMPRINT",EDGE,{"disambiguationData":[TD([[subQ2,-1.0]])],"derivedFrom":subQ1}),-1.0]])]});}
            var Q40;
            {var subQ0=sQuery(id+"F5.wireOp",EDGE,"E23");var subQ5=makeQuery(id+"F5.imprint","INTERSECT",VERTEX,{"derivedFrom":[subQ0,sQuery(id+"F5.wireOp",EDGE,"E37")]});Q40=makeQuery(id+"F5.imprint","IMPRINT",FACE,{"disambiguationData":[TD([[makeQuery(id+"F5.imprint","IMPRINT",EDGE,{"disambiguationData":[TD([[subQ5,1.0]])],"derivedFrom":subQ0}),1.0]])]});}
            var Q41;
            {var subQ0=sQuery(id+"F5.wireOp",EDGE,"E33");var subQ1=sQuery(id+"F5.wireOp",EDGE,"E23");var subQ2=makeQuery(id+"F5.imprint","INTERSECT",VERTEX,{"derivedFrom":[subQ1,subQ0]});Q41=makeQuery(id+"F5.imprint","IMPRINT",FACE,{"disambiguationData":[TD([[makeQuery(id+"F5.imprint","IMPRINT",EDGE,{"disambiguationData":[TD([[subQ2,1.0]])],"derivedFrom":subQ1}),-1.0]])]});}
            var Q42;
            {var subQ0=sQuery(id+"F5.wireOp",EDGE,"E25");var subQ1=sQuery(id+"F5.wireOp",EDGE,"E16");var subQ2=makeQuery(id+"F5.imprint","INTERSECT",VERTEX,{"derivedFrom":[subQ1,subQ0]});Q42=makeQuery(id+"F5.imprint","IMPRINT",FACE,{"disambiguationData":[TD([[makeQuery(id+"F5.imprint","IMPRINT",EDGE,{"disambiguationData":[TD([[subQ2,-1.0]])],"derivedFrom":subQ1}),-1.0]])]});}
            var Q43;
            {var subQ0=sQuery(id+"F5.wireOp",EDGE,"E34");var subQ1=sQuery(id+"F5.wireOp",EDGE,"E25");var subQ2=makeQuery(id+"F5.imprint","INTERSECT",VERTEX,{"derivedFrom":[subQ1,subQ0]});Q43=makeQuery(id+"F5.imprint","IMPRINT",FACE,{"disambiguationData":[TD([[makeQuery(id+"F5.imprint","IMPRINT",EDGE,{"disambiguationData":[TD([[subQ2,-1.0]])],"derivedFrom":subQ1}),-1.0]])]});}
            var Q44;
            {var subQ0=sQuery(id+"F5.wireOp",EDGE,"E35");var subQ1=sQuery(id+"F5.wireOp",EDGE,"E25");var subQ2=makeQuery(id+"F5.imprint","INTERSECT",VERTEX,{"derivedFrom":[subQ1,subQ0]});Q44=makeQuery(id+"F5.imprint","IMPRINT",FACE,{"disambiguationData":[TD([[makeQuery(id+"F5.imprint","IMPRINT",EDGE,{"disambiguationData":[TD([[subQ2,-1.0]])],"derivedFrom":subQ1}),-1.0]])]});}
            var Q45;
            {var subQ0=sQuery(id+"F5.wireOp",EDGE,"E33");var subQ1=sQuery(id+"F5.wireOp",EDGE,"E17");var subQ2=makeQuery(id+"F5.imprint","INTERSECT",VERTEX,{"derivedFrom":[subQ1,subQ0]});Q45=makeQuery(id+"F5.imprint","IMPRINT",FACE,{"disambiguationData":[TD([[makeQuery(id+"F5.imprint","IMPRINT",EDGE,{"disambiguationData":[TD([[subQ2,-1.0]])],"derivedFrom":subQ1}),-1.0]])]});}
            var Q46;
            {var subQ0=sQuery(id+"F5.wireOp",EDGE,"E35");var subQ1=sQuery(id+"F5.wireOp",EDGE,"E17");var subQ2=makeQuery(id+"F5.imprint","INTERSECT",VERTEX,{"derivedFrom":[subQ1,subQ0]});Q46=makeQuery(id+"F5.imprint","IMPRINT",FACE,{"disambiguationData":[TD([[makeQuery(id+"F5.imprint","IMPRINT",EDGE,{"disambiguationData":[TD([[subQ2,-1.0]])],"derivedFrom":subQ1}),-1.0]])]});}
            var Q47;
            {var subQ0=sQuery(id+"F5.wireOp",EDGE,"E36");var subQ1=sQuery(id+"F5.wireOp",EDGE,"E25");var subQ2=makeQuery(id+"F5.imprint","INTERSECT",VERTEX,{"derivedFrom":[subQ1,subQ0]});Q47=makeQuery(id+"F5.imprint","IMPRINT",FACE,{"disambiguationData":[TD([[makeQuery(id+"F5.imprint","IMPRINT",EDGE,{"disambiguationData":[TD([[subQ2,-1.0]])],"derivedFrom":subQ1}),-1.0]])]});}
            var Q48;
            {var subQ0=sQuery(id+"F5.wireOp",EDGE,"E35");var subQ1=sQuery(id+"F5.wireOp",EDGE,"E23");var subQ2=makeQuery(id+"F5.imprint","INTERSECT",VERTEX,{"derivedFrom":[subQ1,subQ0]});Q48=makeQuery(id+"F5.imprint","IMPRINT",FACE,{"disambiguationData":[TD([[makeQuery(id+"F5.imprint","IMPRINT",EDGE,{"disambiguationData":[TD([[subQ2,1.0]])],"derivedFrom":subQ1}),-1.0]])]});}
            var Q49;
            {var subQ0=sQuery(id+"F5.wireOp",EDGE,"E31");var subQ1=sQuery(id+"F5.wireOp",EDGE,"E22");var subQ2=makeQuery(id+"F5.imprint","INTERSECT",VERTEX,{"derivedFrom":[subQ1,subQ0]});Q49=makeQuery(id+"F5.imprint","IMPRINT",FACE,{"disambiguationData":[TD([[makeQuery(id+"F5.imprint","IMPRINT",EDGE,{"disambiguationData":[TD([[subQ2,-1.0]])],"derivedFrom":subQ1}),1.0]])]});}
            var Q50;
            {var subQ0=sQuery(id+"F5.wireOp",EDGE,"E37");var subQ1=sQuery(id+"F5.wireOp",EDGE,"E23");var subQ2=makeQuery(id+"F5.imprint","INTERSECT",VERTEX,{"derivedFrom":[subQ1,subQ0]});Q50=makeQuery(id+"F5.imprint","IMPRINT",FACE,{"disambiguationData":[TD([[makeQuery(id+"F5.imprint","IMPRINT",EDGE,{"disambiguationData":[TD([[subQ2,1.0]])],"derivedFrom":subQ1}),-1.0]])]});}
            var Q51;
            {var subQ0=sQuery(id+"F5.wireOp",EDGE,"E38");var subQ1=sQuery(id+"F5.wireOp",EDGE,"E25");var subQ2=makeQuery(id+"F5.imprint","INTERSECT",VERTEX,{"derivedFrom":[subQ1,subQ0]});Q51=makeQuery(id+"F5.imprint","IMPRINT",FACE,{"disambiguationData":[TD([[makeQuery(id+"F5.imprint","IMPRINT",EDGE,{"disambiguationData":[TD([[subQ2,-1.0]])],"derivedFrom":subQ1}),-1.0]])]});}
            var Q52;
            {var subQ1=sQuery(id+"F5.wireOp",EDGE,"E18");var subQ3=sQuery(id+"F5.wireOp",EDGE,"E26");var subQ4=makeQuery(id+"F5.imprint","INTERSECT",VERTEX,{"derivedFrom":[subQ1,subQ3]});Q52=makeQuery(id+"F5.imprint","IMPRINT",FACE,{"disambiguationData":[TD([[makeQuery(id+"F5.imprint","IMPRINT",EDGE,{"disambiguationData":[TD([[subQ4,1.0]])],"derivedFrom":subQ3}),-1.0]])]});}
            var Q53;
            {var subQ0=sQuery(id+"F5.wireOp",EDGE,"E37");var subQ1=sQuery(id+"F5.wireOp",EDGE,"E25");var subQ2=makeQuery(id+"F5.imprint","INTERSECT",VERTEX,{"derivedFrom":[subQ1,subQ0]});Q53=makeQuery(id+"F5.imprint","IMPRINT",FACE,{"disambiguationData":[TD([[makeQuery(id+"F5.imprint","IMPRINT",EDGE,{"disambiguationData":[TD([[subQ2,-1.0]])],"derivedFrom":subQ1}),-1.0]])]});}
            var Q54;
            {var subQ0=sQuery(id+"F5.wireOp",EDGE,"E37");var subQ1=sQuery(id+"F5.wireOp",EDGE,"E17");var subQ2=makeQuery(id+"F5.imprint","INTERSECT",VERTEX,{"derivedFrom":[subQ1,subQ0]});Q54=makeQuery(id+"F5.imprint","IMPRINT",FACE,{"disambiguationData":[TD([[makeQuery(id+"F5.imprint","IMPRINT",EDGE,{"disambiguationData":[TD([[subQ2,-1.0]])],"derivedFrom":subQ1}),-1.0]])]});}
            extrude(context, id + "F6", {"entities" : qUnion([Q0, Q1, Q2, Q3, Q4, Q5, Q6, Q7, Q8, Q9, Q10, Q11, Q12, Q13, Q14, Q15, Q16, Q17, Q18, Q19, Q20, Q21, Q22, Q23, Q24, Q25, Q26, Q27, Q28, Q29, Q30, Q31, Q32, Q33, Q34, Q35, Q36, Q37, Q38, Q39, Q40, Q41, Q42, Q43, Q44, Q45, Q46, Q47, Q48, Q49, Q50, Q51, Q52, Q53, Q54]), "operationType" : NewBodyOperationType.REMOVE, "oppositeDirection" : true, "depth" : 0.5 * mm});
        }
    });
